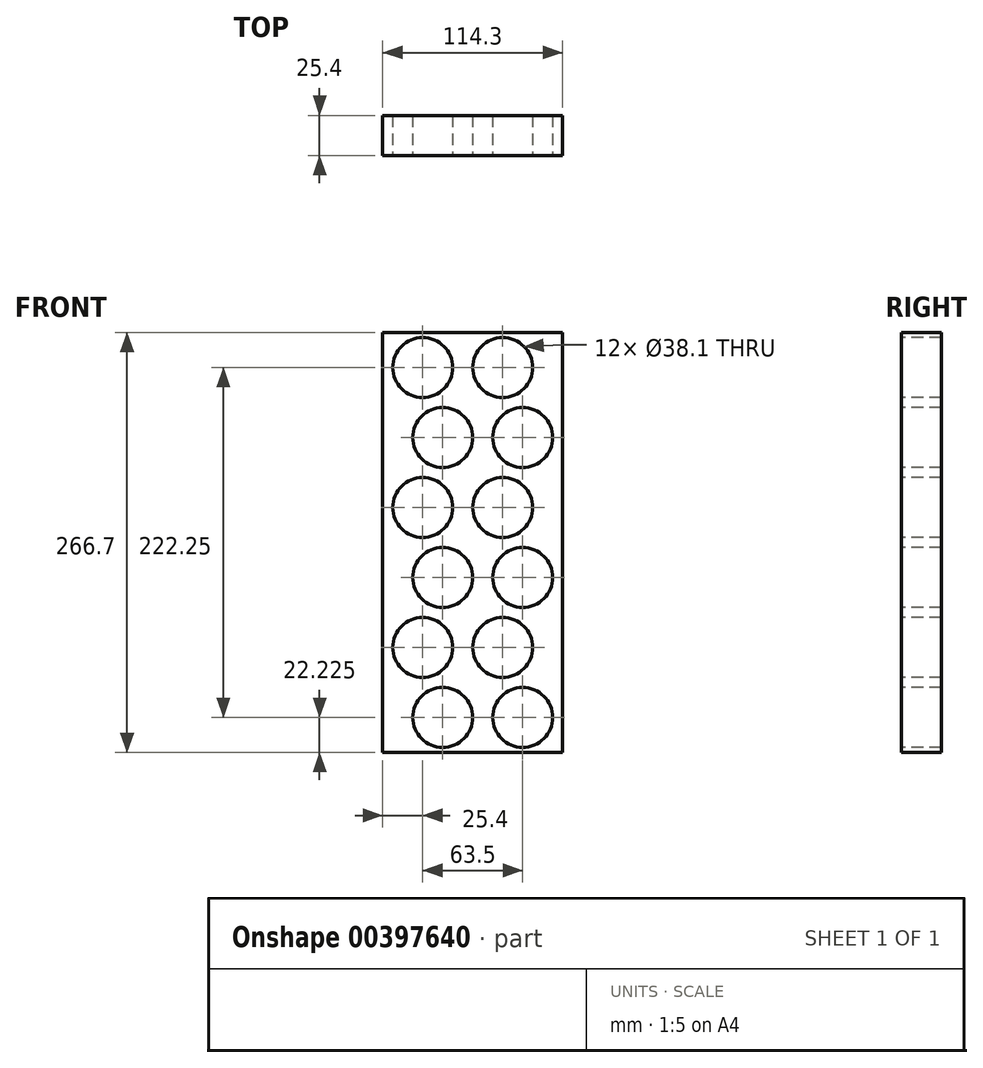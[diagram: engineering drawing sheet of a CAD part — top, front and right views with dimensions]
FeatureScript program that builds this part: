
annotation { "Feature Type Name" : "Feature", "Feature Type Description" : "" }
export const myFeature = defineFeature(function(context is Context, id is Id, definition is map)
    precondition{}
    {
        {
            var Q0;
            Q0=qCreatedBy(makeId("Front.planeOp"),FACE);
            var sketch = newSketch(context, id + "F0", { "sketchPlane" : qUnion([Q0])});
            skLineSegment(sketch, "E0.bottom", {"start": v(0, 0) * mm, "end": v(-114.3, 0) * mm});
            skLineSegment(sketch, "E0.top", {"start": v(0, 266.7) * mm, "end": v(-114.3, 266.7) * mm});
            skLineSegment(sketch, "E0.left", {"start": v(0, 0) * mm, "end": v(0, 266.7) * mm});
            skLineSegment(sketch, "E0.right", {"start": v(-114.3, 0) * mm, "end": v(-114.3, 266.7) * mm});
            skSolve(sketch);
        }
        {
            var Q0;
            Q0 = qSketchRegion(id + "F0", true);
            extrude(context, id + "F1", {"entities" : qUnion([Q0]), "depth" : 25.4 * mm});
        }
        {
            var Q0;
            Q0=makeQuery(id+"F1.opExtrude","CAP_FACE",FACE,{"disambiguationData":[OSD([sQuery(id+"F0.wireOp",EDGE,"E0.bottom"),sQuery(id+"F0.wireOp",EDGE,"E0.top"),sQuery(id+"F0.wireOp",EDGE,"E0.left"),sQuery(id+"F0.wireOp",EDGE,"E0.right")])],"isStart":false});
            var sketch = newSketch(context, id + "F2", { "sketchPlane" : qUnion([Q0])});
            skLineSegment(sketch, "E1", {"start": v(0, 0) * mm, "end": v(-57.15, 0) * mm});
            skLineSegment(sketch, "E2", {"start": v(0, 0) * mm, "end": v(-28.58, 0) * mm});
            skLineSegment(sketch, "E3", {"start": v(0, 0) * mm, "end": v(-85.73, 0) * mm});
            skCircle(sketch, "E4", {"center": v(-25.4, 22.23) * mm, "radius": 19.05 * mm});
            skLineSegment(sketch, "E5", {"start": v(0, 0) * mm, "end": v(0, 22.22) * mm});
            skLineSegment(sketch, "E6", {"start": v(0, 22.23) * mm, "end": v(-25.4, 22.22) * mm});
            skLineSegment(sketch, "E7", {"start": v(0, 22.22) * mm, "end": v(-76.2, 22.22) * mm});
            skCircle(sketch, "E8", {"center": v(-76.2, 22.22) * mm, "radius": 19.05 * mm});
            skLineSegment(sketch, "E9", {"start": v(-114.3, 0) * mm, "end": v(-114.3, 66.68) * mm});
            skLineSegment(sketch, "E10", {"start": v(-114.3, 66.68) * mm, "end": v(-88.9, 66.68) * mm});
            skLineSegment(sketch, "E11", {"start": v(-114.3, 66.68) * mm, "end": v(-38.1, 66.68) * mm});
            skPoint(sketch, "E11.endSnap0", {"position": v(-101.6, 66.68) * mm});
            skCircle(sketch, "E12", {"center": v(-88.9, 66.68) * mm, "radius": 19.05 * mm});
            skCircle(sketch, "E13", {"center": v(-38.1, 66.68) * mm, "radius": 19.05 * mm});
            skCircle(sketch, "E14.0.1.0", {"center": v(-25.4, 111.12) * mm, "radius": 19.05 * mm});
            skCircle(sketch, "E14.0.1.1", {"center": v(-76.2, 111.12) * mm, "radius": 19.05 * mm});
            skCircle(sketch, "E14.0.2.0", {"center": v(-25.4, 200.03) * mm, "radius": 19.05 * mm});
            skCircle(sketch, "E14.0.2.1", {"center": v(-76.2, 200.03) * mm, "radius": 19.05 * mm});
            skLineSegment(sketch, "E14.direction1", {"start": v(-76.2, 22.22) * mm, "end": v(-50.8, 22.22) * mm, "construction": true});
            skLineSegment(sketch, "E14.direction2", {"start": v(-76.2, 22.22) * mm, "end": v(-76.2, 111.12) * mm, "construction": true});
            skCircle(sketch, "E15.0.1.0", {"center": v(-38.1, 155.58) * mm, "radius": 19.05 * mm});
            skCircle(sketch, "E15.0.1.1", {"center": v(-88.9, 155.57) * mm, "radius": 19.05 * mm});
            skCircle(sketch, "E15.0.2.0", {"center": v(-38.1, 244.47) * mm, "radius": 19.05 * mm});
            skCircle(sketch, "E15.0.2.1", {"center": v(-88.9, 244.47) * mm, "radius": 19.05 * mm});
            skLineSegment(sketch, "E15.direction1", {"start": v(-38.1, 66.68) * mm, "end": v(-12.7, 66.68) * mm, "construction": true});
            skLineSegment(sketch, "E15.direction2", {"start": v(-38.1, 66.68) * mm, "end": v(-38.1, 155.58) * mm, "construction": true});
            skSolve(sketch);
        }
        {
            var Q0;
            Q0 = qSketchRegion(id + "F2", true);
            extrude(context, id + "F3", {"entities" : qUnion([Q0]), "operationType" : NewBodyOperationType.REMOVE, "oppositeDirection" : true, "depth" : 25.4 * mm});
        }
    });
